AUTODESK INVENTOR PART (.ipt)
format: ipt  version: 2015 (Build 190159000, 159)  size: 125,952 bytes
history: native  units: in
note: dims shown in document units (in); Inventor stores cm internally (conversion verified against a paired STEP export)
features: sketch x3, other x1
ambient origin geometry x8: Origin, YZ Plane, XZ Plane, XY Plane, X Axis, Y Axis, Z Axis, Center Point
feature tree (4):
  other  "50cal_geometrysketch.ipt"
  sketch  "Sketch3"  dims[d2=3.5433in d8=0.1693in d9=0.1693in d10=0.1693in d17=1.5in d20=45.0deg d24=1.2461in d26=1.1811in d28=0.5906in d29=0.5906in d39=0.0591in d44=1.2461in d45=0.375in d46=0.201in d48=0.201in d49=0.25in d50=0.19in d51=0.19in d54=0.125in d55=0.125in]
  sketch  "Sketch2"  dims[d1=0.7087in]
  sketch  "Sketch1"  dims[d0=0.3937in]
